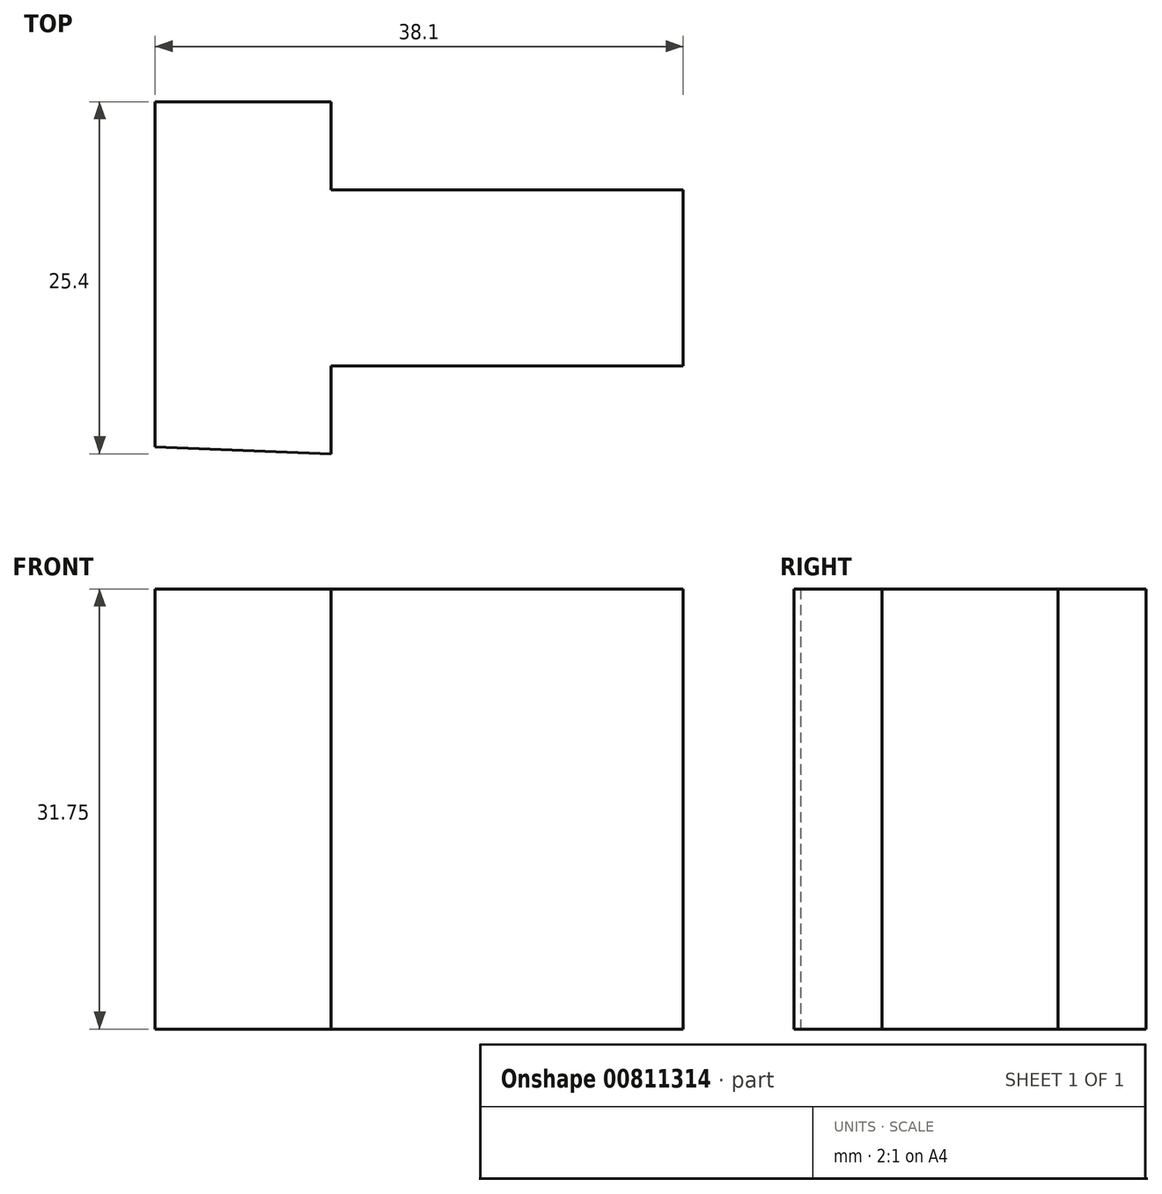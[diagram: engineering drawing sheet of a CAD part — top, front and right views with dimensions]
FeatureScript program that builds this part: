
annotation { "Feature Type Name" : "Feature", "Feature Type Description" : "" }
export const myFeature = defineFeature(function(context is Context, id is Id, definition is map)
    precondition{}
    {
        {
            var Q0;
            Q0=qCreatedBy(makeId("Top.planeOp"),FACE);
            var sketch = newSketch(context, id + "F0", { "sketchPlane" : qUnion([Q0])});
            skLineSegment(sketch, "E0", {"start": v(0, 0) * mm, "end": v(0, 25.4) * mm});
            skLineSegment(sketch, "E1", {"start": v(0, 25.4) * mm, "end": v(12.7, 25.4) * mm});
            skLineSegment(sketch, "E2", {"start": v(12.7, 25.4) * mm, "end": v(6.35, 25.4) * mm});
            skLineSegment(sketch, "E3", {"start": v(12.7, 25.4) * mm, "end": v(12.7, 19.05) * mm});
            skLineSegment(sketch, "E4", {"start": v(12.7, 19.05) * mm, "end": v(38.1, 19.05) * mm});
            skLineSegment(sketch, "E5", {"start": v(38.1, 19.05) * mm, "end": v(38.1, 6.35) * mm});
            skLineSegment(sketch, "E6", {"start": v(38.1, 6.35) * mm, "end": v(12.7, 6.35) * mm});
            skLineSegment(sketch, "E7", {"start": v(12.7, 6.35) * mm, "end": v(12.7, 0) * mm});
            skLineSegment(sketch, "E8", {"start": v(12.7, 0) * mm, "end": v(-0.1, 0.49) * mm});
            skSolve(sketch);
        }
        {
            var Q0;
            Q0 = qSketchRegion(id + "F0", true);
            extrude(context, id + "F1", {"entities" : qUnion([Q0]), "depth" : 31.75 * mm, "offsetDistance" : 25.4 * mm});
        }
    });
